# Revit family: Emergency_Equipment-Tepid-Wall_Mounted_Combination_Shower-S5530
name_source: partatom
category: Plumbing Fixtures
revit_build: Autodesk Revit Architecture 2016 (Build: 20150220_1215(x64)
units: mm (PartAtom-declared; Revit-internal decimal feet)

## family parameters
Always vertical = No
Cut with Voids When Loaded = No
OmniClass Number = 23.45.05.14.24
OmniClass Title = Eye Wash Fountains
Part Type = Normal
Room Calculation Point = No
Round Connector Dimension = Use Diameter
Shared = No
Work Plane-Based = Yes

## types (1)
- Emergency_Equipment-Tepid-Wall_Mounted_Combination_Shower-S5530
    AB Bowl = Yes
    AB Showerhead = Yes
    Bowl Material = Plastic - Stingray - ABS AB
    C Pipe = 2.56 "
    CW Connection = Yes
    Default Elevation = 48 "
    Description = Wall Mounted Emergency Shower and Eye-Face Wash
    Dimension Disclaimer = Dimensions are ±0.50”. Design and specifications are subject to change without notice.
    Drain Connection = 1"
    Filter = No
    HW Connection = Yes
    Height = 69.6 "
    Length = 37 "
    Manufacturer = Stingray Systems
    Model = S5530-GA-NFT-ABAB
    Mount Height = 27 "
    Pipe Finish = Metal - Stingray - Galvanized GA
    Product Documentation Link = http://www.tepid.com
    Product Name = Standard Wall Mounted Combination Emergency Shower and Eye-Face Wash
    Product Page URL = http://www.tepid.com
    SS Bowl = No
    SS Showerhead = No
    Shower Pull Height = 40.2 "
    Showerhead Material = Plastic - Stingray - ABS AB
    Supply Connection = 1"
    URL = www.tepid.com
    Vent Connection = No
    Version = 2016-v1.0a
    Waste Connection = Yes
    Width = 16.3 "

## geometry (parser evidence)
native form markers: Sweep x16
no freeform markers — native parametric forms only
